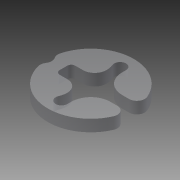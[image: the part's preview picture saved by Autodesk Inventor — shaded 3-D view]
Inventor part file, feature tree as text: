
AUTODESK INVENTOR PART (.ipt)
format: ipt  version: 2015 (Build 190159000, 159)  size: 142,848 bytes
history: native  units: mm
features: extrude x1
ambient origin geometry x8: Origin, YZ Plane, XZ Plane, XY Plane, X Axis, Y Axis, Z Axis, Center Point
bodies: Body1 (feature_tree)
feature tree (1):
  extrude  "Extrusion2"  Depth=5.0mm
